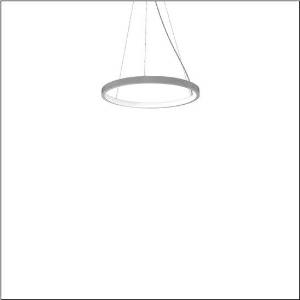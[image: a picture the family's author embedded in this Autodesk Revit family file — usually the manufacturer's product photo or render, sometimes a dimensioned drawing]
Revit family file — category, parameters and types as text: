
# Revit family: silica_21_ring-i_5pjbi1d3204a
name_source: partatom
category: Lighting Fixtures
units: mm (PartAtom-declared; Revit-internal decimal feet)

## family parameters
Cut with Voids When Loaded = No
Host = Face
Light Source = No
Part Type = Normal
Room Calculation Point = No
Round Connector Dimension = Use Diameter
Shared = No

## types (1)
- Silica 21 Ring-I (1 x LED, 3510 lm, 60 W, 4000K)
    Apparent Load = 60 VA
    CIE Flux Codes = 22 48 76 50 101
    Color Rendering = 80
    Color Temperature = 4000K
    Default Elevation = 1800 mm
    Description = Silica 21 Ring-I, suspended luminaire, of PMMA, frosted, light emission: inner ring side luminous distribution, primary light characteristic: symmetric, installation type: suspended mounting, LED, rated luminous flux: 3.510lm, luminous efficacy: 59lm/W, light colour: 840, colour temperature: 4000K, control gear: DALI 2, with terminal, 5-pole, mains connection: 230V, AC/DC, 0/50..60Hz, rated input power: 60W, housing, of extruded aluminium section, metallic grey (RAL 9006), diameter: 610mm, ceiling canopy, metallic grey (RAL 9006), protection rating (lamp compartment): IP40, insulation class (complete): insulation class I (protective earthing), certification: CE, impact resistance: IK02, permissible operating ambient temperature: 0..+35°C, packaging unit: 1 piece
    Height = 48 mm  [stored 0.15748 ft]
    Lamp = 1 x LED
    Lamp Light Flux = 3510 lm
    Lamp Power = 60 W
    Lamp count = 1
    Length = 610 mm
    Luminous efficacy = 59 lm/W
    Manufacturer = Siteco
    ModVariant = No
    Model = 5PJBI1D3204A
    Mounting Place = Ceiling
    Mounting Type = Pendant
    Number of Poles = 1
    OnlyDefault = Yes
    Power Factor = 1
    Product Name = Silica 21 Ring-I
    Product group = suspended luminaire
    ProductGroupID = 904
    Protection Class = Protection class I
    Protection Degree = IP 40
    RLX_Detail_Level = 1
    RLX_Emergency_Light_Flux = 0 lm
    RLX_Emergency_Type = 0
    RLX_Emergency_Type_DB = No
    RlxData = <blob elided: 11497 chars, md5=09e17df3>
    Socket = socket
    Standby Power = 0 W
    System Light Flux = 3510 lm
    System Power = 60 W
    Type Comments = Product without accessories
    Type Image = l_1251750.jpg
    URL = http://relux.com
    VarID = ---
    Voltage = 0 V
    Weight = 0.00 kg
    Width = 0 mm  [stored 0 ft]

note: [stored X ft] marks values corroborated as IEEE doubles in the binary element streams (Revit-internal decimal feet)

## geometry (parser evidence)
native form markers: Sweep x10
no freeform markers — native parametric forms only
